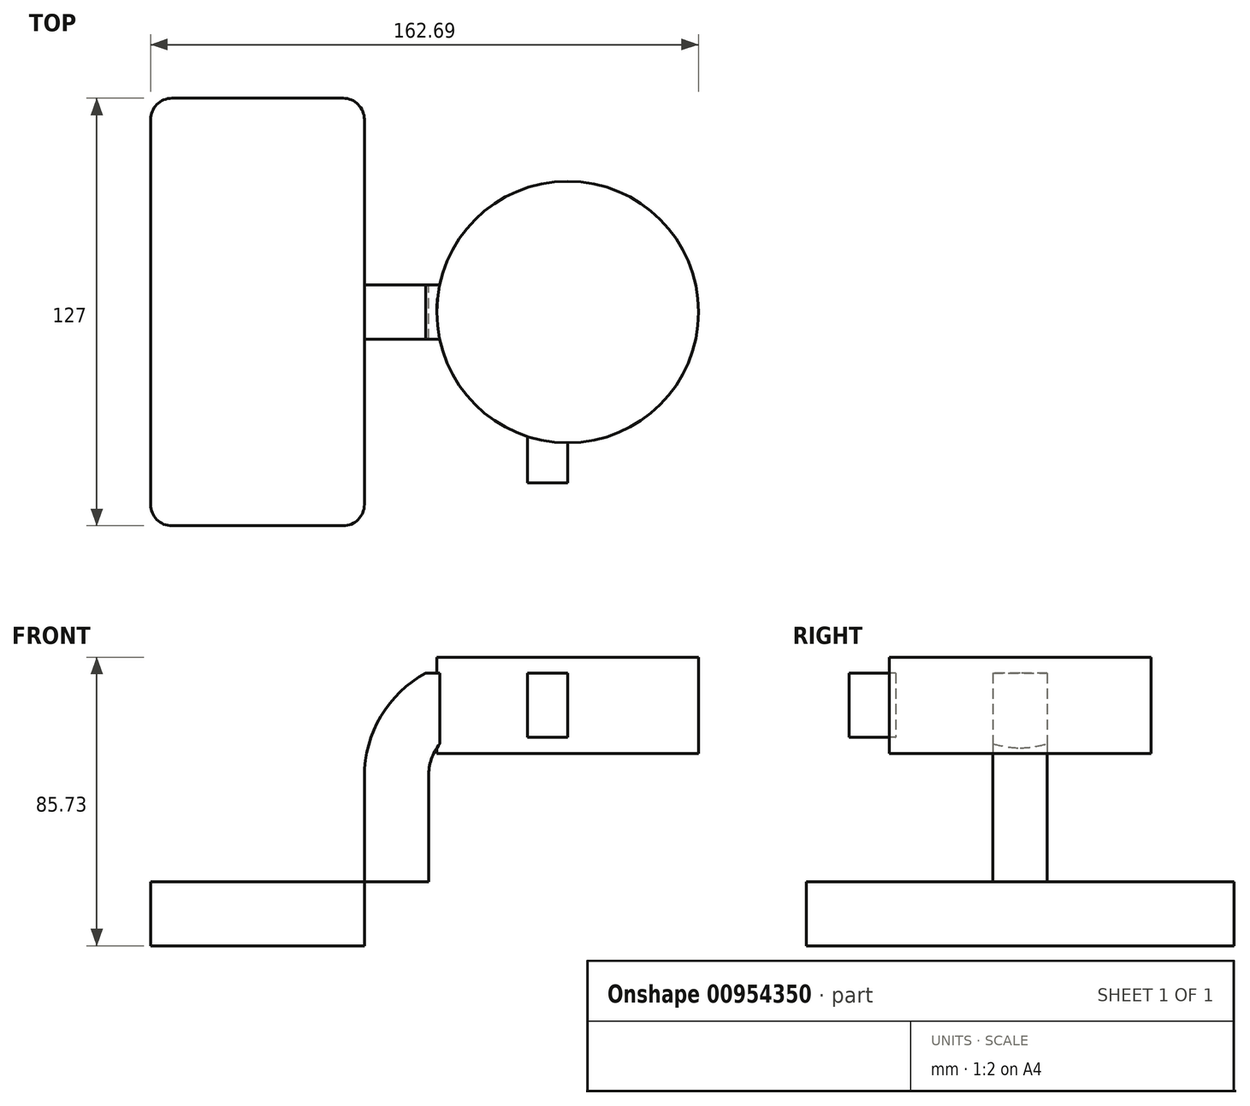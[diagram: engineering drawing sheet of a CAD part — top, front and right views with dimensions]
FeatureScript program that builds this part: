
annotation { "Feature Type Name" : "Feature", "Feature Type Description" : "" }
export const myFeature = defineFeature(function(context is Context, id is Id, definition is map)
    precondition{}
    {
        {
            var Q0;
            Q0=qCreatedBy(makeId("Front.planeOp"),FACE);
            var sketch = newSketch(context, id + "F0", { "sketchPlane" : qUnion([Q0])});
            skLineSegment(sketch, "E0.bottom", {"start": v(-41.28, 9.52) * mm, "end": v(41.28, 9.52) * mm});
            skLineSegment(sketch, "E0.top", {"start": v(-41.28, -9.52) * mm, "end": v(41.28, -9.52) * mm});
            skLineSegment(sketch, "E0.left", {"start": v(-41.28, 9.52) * mm, "end": v(-41.28, -9.52) * mm});
            skLineSegment(sketch, "E0.right", {"start": v(41.28, 9.52) * mm, "end": v(41.28, -9.52) * mm});
            skPoint(sketch, "E0.middle", {"position": v(0, 0) * mm});
            skLineSegment(sketch, "E1.bottom", {"start": v(70.62, 47.62) * mm, "end": v(121.42, 47.62) * mm});
            skLineSegment(sketch, "E1.top", {"start": v(70.62, 76.2) * mm, "end": v(121.42, 76.2) * mm});
            skLineSegment(sketch, "E1.left", {"start": v(70.62, 47.62) * mm, "end": v(70.62, 76.2) * mm});
            skLineSegment(sketch, "E1.right", {"start": v(121.42, 47.62) * mm, "end": v(121.42, 76.2) * mm});
            skPoint(sketch, "E1.middle", {"position": v(96.02, 61.91) * mm});
            skLineSegment(sketch, "E2", {"start": v(41.28, -9.52) * mm, "end": v(41.28, 40.79) * mm});
            skArc(sketch, "E3", {"start": v(41.27, 40.79) * mm, "mid": v(42.6, 47.12) * mm, "end": v(46.33, 52.4) * mm});
            skLineSegment(sketch, "E4", {"start": v(46.33, 52.4) * mm, "end": v(82.85, 52.4) * mm});
            skLineSegment(sketch, "E5.0", {"start": v(40.43, 71.45) * mm, "end": v(82.85, 71.45) * mm});
            skArc(sketch, "E5.1", {"start": v(22.23, 40.79) * mm, "mid": v(27.12, 58.62) * mm, "end": v(40.43, 71.45) * mm});
            skLineSegment(sketch, "E5.2", {"start": v(22.23, -9.53) * mm, "end": v(22.23, 40.79) * mm});
            skLineSegment(sketch, "E6", {"start": v(82.57, 47.62) * mm, "end": v(82.57, 76.2) * mm});
            skFitSpline(sketch, "E7", {"points": [v(-41.28, 9.52) * mm, v(40.43, 71.45) * mm], "startDerivative": vector(-31.1, 86.22) * mm, "endDerivative": vector(104.59, -21) * mm});
            skSolve(sketch);
        }
        {
            var Q0;
            {var subQ0=sQuery(id+"F0.wireOp",EDGE,"E0.left");Q0=makeQuery(id+"F0.imprint","IMPRINT",FACE,{"disambiguationData":[TD([[makeQuery(id+"F0.imprint","IMPRINT",EDGE,{"derivedFrom":subQ0}),1.0]])]});}
            extrude(context, id + "F1", {"entities" : qUnion([Q0]), "endBound" : BoundingType.SYMMETRIC, "depth" : 127 * mm, "offsetDistance" : 25.4 * mm});
        }
        {
            var Q0;
            {var subQ3=sQuery(id+"F0.wireOp",EDGE,"E3");Q0=makeQuery(id+"F0.imprint","IMPRINT",FACE,{"disambiguationData":[TD([[makeQuery(id+"F0.imprint","IMPRINT",EDGE,{"derivedFrom":subQ3}),1.0]])]});}
            var Q1;
            {var subQ0=sQuery(id+"F0.wireOp",EDGE,"E4");var subQ1=sQuery(id+"F0.wireOp",EDGE,"E1.left");var subQ2=makeQuery(id+"F0.imprint","INTERSECT",VERTEX,{"derivedFrom":[subQ1,subQ0]});Q1=makeQuery(id+"F0.imprint","IMPRINT",FACE,{"disambiguationData":[TD([[makeQuery(id+"F0.imprint","IMPRINT",EDGE,{"disambiguationData":[TD([[subQ2,-1.0]])],"derivedFrom":subQ1}),-1.0]])]});}
            extrude(context, id + "F2", {"entities" : qUnion([Q0, Q1]), "depth" : 50.8 * mm, "offsetDistance" : 25.4 * mm});
        }
        {
            var Q0;
            {var subQ4=sQuery(id+"F0.wireOp",EDGE,"E5.1");Q0=makeQuery(id+"F0.imprint","IMPRINT",FACE,{"disambiguationData":[TD([[makeQuery(id+"F0.imprint","IMPRINT",EDGE,{"derivedFrom":subQ4}),1.0]])]});}
            extrude(context, id + "F3", {"entities" : qUnion([Q0]), "endBound" : BoundingType.SYMMETRIC, "depth" : 16.13 * mm, "offsetDistance" : 25.4 * mm});
        }
        {
            var Q0;
            {var subQ0=sQuery(id+"F0.wireOp",EDGE,"E1.right");Q0=makeQuery(id+"F0.imprint","IMPRINT",FACE,{"disambiguationData":[TD([[makeQuery(id+"F0.imprint","IMPRINT",EDGE,{"derivedFrom":subQ0}),1.0]])]});}
            var Q1;
            Q1=sQuery(id+"F0.wireOp",EDGE,"E6");
            revolve(context, id + "F4", {"operationType" : NewBodyOperationType.ADD, "surfaceOperationType" : NewSurfaceOperationType.NEW, "entities" : qUnion([Q0]), "axis" : qUnion([Q1]), "revolveType" : RevolveType.FULL});
        }
        {
            var Q0;
            Q0=makeQuery(id+"F1.opExtrude","CAP_EDGE",EDGE,{"disambiguationData":[OSD([sQuery(id+"F0.wireOp",EDGE,"E5.2")])],"isStart":false});
            var Q1;
            Q1=makeQuery(id+"F1.opExtrude","CAP_EDGE",EDGE,{"disambiguationData":[OSD([sQuery(id+"F0.wireOp",EDGE,"E0.left")])],"isStart":false});
            var Q2;
            Q2=makeQuery(id+"F1.opExtrude","CAP_EDGE",EDGE,{"disambiguationData":[OSD([sQuery(id+"F0.wireOp",EDGE,"E0.left")])],"isStart":true});
            var Q3;
            Q3=makeQuery(id+"F1.opExtrude","CAP_EDGE",EDGE,{"disambiguationData":[OSD([sQuery(id+"F0.wireOp",EDGE,"E5.2")])],"isStart":true});
            fillet(context, id + "F5", {"entities" : qUnion([Q0, Q1, Q2, Q3]), "radius" : 6.35 * mm, "tangentPropagation" : true, "allowEdgeOverflow" : false});
        }
    });
